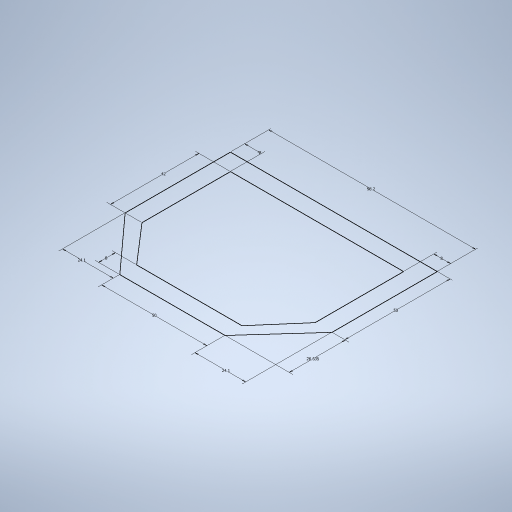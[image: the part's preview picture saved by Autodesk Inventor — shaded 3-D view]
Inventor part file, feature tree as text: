
AUTODESK INVENTOR PART (.ipt)
format: ipt  version: 2024.2 (Build 282272000, 272)  size: 244,224 bytes
history: native  units: mm
features: sketch x1
ambient origin geometry x8: Origin, YZ Plane, XZ Plane, XY Plane, X Axis, Y Axis, Z Axis, Center Point
feature tree (1):
  sketch  "Sketch1"  dims[d0=98.2mm d1=50.0mm d2=50.0mm d5=26.635mm d6=24.1mm d7=24.1mm d8=8.0mm d9=8.0mm d10=8.0mm d11=42.0mm]
